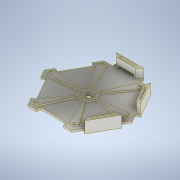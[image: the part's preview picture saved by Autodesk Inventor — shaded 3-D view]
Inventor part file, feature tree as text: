
AUTODESK INVENTOR PART (.ipt)
format: ipt  version: 2020 (Build 240168000, 168)  size: 373,248 bytes
history: native  units: mm
features: extrude x6, sketch x1, pattern_circular x1
ambient origin geometry x8: Origin, YZ Plane, XZ Plane, XY Plane, X Axis, Y Axis, Z Axis, Center Point
bodies: Body1 (feature_tree)
feature tree (8):
  sketch  "Sketch6"  dims[d72=6.5mm d87=15.0mm d88=6.5mm d91=2.5mm d92=2.5mm d95=1.25mm d96=25.0mm d97=2.5mm d98=25.0mm d99=135.0deg d100=0.0mm d105=30.0mm d106=3.0mm d107=0.0mm d108=6.5mm d111=45.0deg d112=15.0mm d113=2.0mm d114=12.5mm d115=2.5mm d116=25.0mm d118=70.0mm d119=54.121778mm d120=1.25mm d121=15.0mm d122=0.0mm d125=5.0mm d126=0.0mm d127=2.0mm d130=7.0mm d131=2.0mm d132=0.0mm d133=60.0mm d134=360.0deg d136=4.0mm d138=3.0mm d139=3.0mm d140=9.25mm d141=0.0mm d142=20.0mm d143=30.0mm d144=7.0mm d145=6.0mm d146=4.0mm d147=10.0mm d148=0.0mm d128=0.872665mm]
  extrude  "Plate"  Depth=15.0mm
  extrude  "Cazzetti"  Depth=6.5mm
  extrude  "ScavoStrip"  Depth=2.5mm
  extrude  "ScalinoAllineamento"  Depth=2.5mm
  extrude  "Foro"  Depth=10.0mm
  pattern_circular  "ScalinoCircolare"  [2 undecoded]
  extrude  "Extrusion15"  Depth=2.5mm
note: 2 required parameter values undecoded (feature->parameter linkage not recoverable at this tier; creation-order binding heuristic only, values carry confidence <= 0.55)
